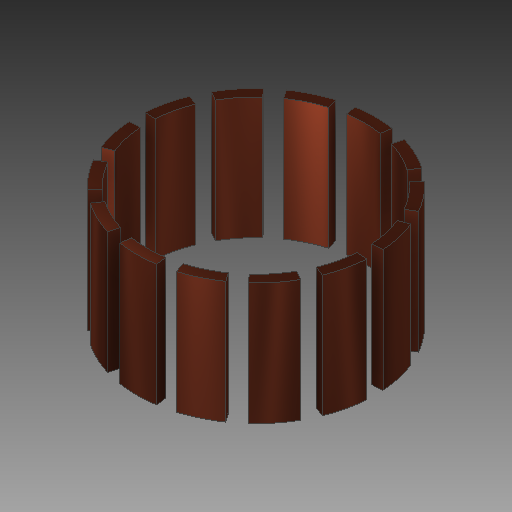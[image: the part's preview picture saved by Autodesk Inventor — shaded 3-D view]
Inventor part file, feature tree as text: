
AUTODESK INVENTOR PART (.ipt)
format: ipt  version: 2019.3 (Build 233278000, 278)  size: 203,264 bytes
history: native  units: mm
features: plane x1
ambient origin geometry x8: Origin, YZ Plane, XZ Plane, XY Plane, X Axis, Y Axis, Z Axis, Center Point
bodies: Solid1 (feature_tree), Solid2 (feature_tree), Solid3 (feature_tree), Solid4 (feature_tree), Solid5 (feature_tree), Solid6 (feature_tree), Solid7 (feature_tree), Solid8 (feature_tree), Solid9 (feature_tree), Solid10 (feature_tree), Solid11 (feature_tree), Solid12 (feature_tree), Solid13 (feature_tree), Solid14 (feature_tree), Body15 (feature_tree), Body16 (feature_tree), Body17 (feature_tree), Body18 (feature_tree), Body19 (feature_tree), Body20 (feature_tree), Body21 (feature_tree), Body22 (feature_tree), Body23 (feature_tree), Body24 (feature_tree), Body25 (feature_tree), Body26 (feature_tree), Body27 (feature_tree), Body28 (feature_tree)
feature tree (1):
  plane  "Work Plane1"
